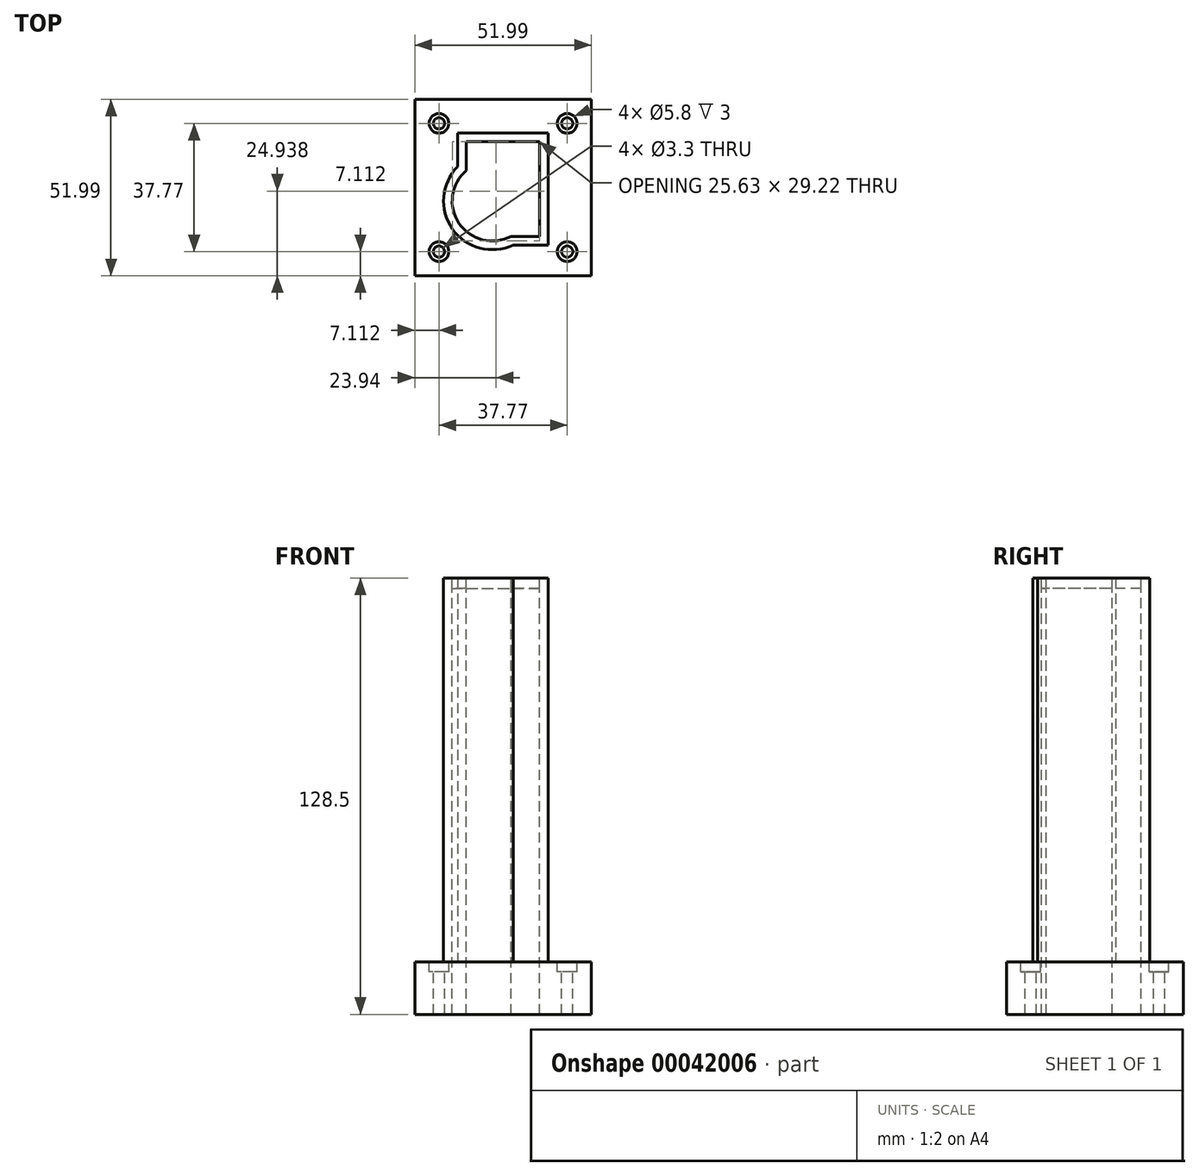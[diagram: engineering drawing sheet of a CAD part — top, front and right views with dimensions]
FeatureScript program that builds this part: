
annotation { "Feature Type Name" : "Feature", "Feature Type Description" : "" }
export const myFeature = defineFeature(function(context is Context, id is Id, definition is map)
    precondition{}
    {
        {
            var Q0;
            Q0=qCreatedBy(makeId("Top.planeOp"),FACE);
            var sketch = newSketch(context, id + "F0", { "sketchPlane" : qUnion([Q0])});
            skLineSegment(sketch, "E0.bottom", {"start": v(0, 0) * mm, "end": v(52, 0) * mm});
            skLineSegment(sketch, "E0.top", {"start": v(0, 52) * mm, "end": v(52, 52) * mm});
            skLineSegment(sketch, "E0.left", {"start": v(0, 0) * mm, "end": v(0, 52) * mm});
            skLineSegment(sketch, "E0.right", {"start": v(52, 0) * mm, "end": v(52, 52) * mm});
            skSolve(sketch);
        }
        {
            var Q0;
            Q0=qSketchRegion(id+"F0",true);
            extrude(context, id + "F1", {"entities" : qUnion([Q0]), "depth" : 15.5 * mm});
        }
        {
            var Q0;
            Q0=makeQuery(id+"F1.opExtrude","CAP_FACE",FACE,{"disambiguationData":[OSD([sQuery(id+"F0.wireOp",EDGE,"E0.bottom"),sQuery(id+"F0.wireOp",EDGE,"E0.top"),sQuery(id+"F0.wireOp",EDGE,"E0.left"),sQuery(id+"F0.wireOp",EDGE,"E0.right")])],"isStart":false});
            var sketch = newSketch(context, id + "F2", { "sketchPlane" : qUnion([Q0])});
            skCircle(sketch, "E1", {"center": v(7.11, 44.88) * mm, "radius": 2.9 * mm});
            skCircle(sketch, "E2", {"center": v(44.88, 44.88) * mm, "radius": 2.9 * mm});
            skCircle(sketch, "E3", {"center": v(7.11, 7.11) * mm, "radius": 2.9 * mm});
            skCircle(sketch, "E4", {"center": v(44.88, 7.11) * mm, "radius": 2.9 * mm});
            skSolve(sketch);
        }
        {
            var Q0;
            Q0=qSketchRegion(id+"F2",true);
            extrude(context, id + "F3", {"entities" : qUnion([Q0]), "operationType" : NewBodyOperationType.REMOVE, "oppositeDirection" : true, "depth" : 3 * mm});
        }
        {
            var Q0;
            Q0=makeQuery(id+"F3.boolean.opBoolean","COPY",FACE,{"derivedFrom":makeQuery(id+"F3.opExtrude","CAP_FACE",FACE,{"disambiguationData":[OSD([sQuery(id+"F2.wireOp",EDGE,"E1")])],"isStart":false})});
            var sketch = newSketch(context, id + "F4", { "sketchPlane" : qUnion([Q0])});
            skCircle(sketch, "E5", {"center": v(7.11, 44.88) * mm, "radius": 1.65 * mm});
            skSolve(sketch);
        }
        {
            var Q0;
            Q0=qSketchRegion(id+"F4",true);
            extrude(context, id + "F5", {"entities" : qUnion([Q0]), "operationType" : NewBodyOperationType.REMOVE, "endBound" : BoundingType.THROUGH_ALL, "oppositeDirection" : true, "depth" : 25.4 * mm});
        }
        {
            var Q0;
            Q0=makeQuery(id+"F3.boolean.opBoolean","COPY",FACE,{"derivedFrom":makeQuery(id+"F3.opExtrude","CAP_FACE",FACE,{"disambiguationData":[OSD([sQuery(id+"F2.wireOp",EDGE,"E2")])],"isStart":false})});
            var sketch = newSketch(context, id + "F6", { "sketchPlane" : qUnion([Q0])});
            skCircle(sketch, "E6", {"center": v(44.88, 44.88) * mm, "radius": 1.65 * mm});
            skSolve(sketch);
        }
        {
            var Q0;
            Q0=qSketchRegion(id+"F6",true);
            extrude(context, id + "F7", {"entities" : qUnion([Q0]), "operationType" : NewBodyOperationType.REMOVE, "endBound" : BoundingType.THROUGH_ALL, "oppositeDirection" : true, "depth" : 25.4 * mm});
        }
        {
            var Q0;
            Q0=makeQuery(id+"F3.boolean.opBoolean","COPY",FACE,{"derivedFrom":makeQuery(id+"F3.opExtrude","CAP_FACE",FACE,{"disambiguationData":[OSD([sQuery(id+"F2.wireOp",EDGE,"E3")])],"isStart":false})});
            var sketch = newSketch(context, id + "F8", { "sketchPlane" : qUnion([Q0])});
            skCircle(sketch, "E7", {"center": v(7.11, 7.11) * mm, "radius": 1.65 * mm});
            skSolve(sketch);
        }
        {
            var Q0;
            Q0=qSketchRegion(id+"F8",true);
            extrude(context, id + "F9", {"entities" : qUnion([Q0]), "operationType" : NewBodyOperationType.REMOVE, "endBound" : BoundingType.THROUGH_ALL, "oppositeDirection" : true, "depth" : 25.4 * mm});
        }
        {
            var Q0;
            Q0=makeQuery(id+"F3.boolean.opBoolean","COPY",FACE,{"derivedFrom":makeQuery(id+"F3.opExtrude","CAP_FACE",FACE,{"disambiguationData":[OSD([sQuery(id+"F2.wireOp",EDGE,"E4")])],"isStart":false})});
            var sketch = newSketch(context, id + "F10", { "sketchPlane" : qUnion([Q0])});
            skCircle(sketch, "E8", {"center": v(44.88, 7.11) * mm, "radius": 1.65 * mm});
            skSolve(sketch);
        }
        {
            var Q0;
            Q0=qSketchRegion(id+"F10",true);
            extrude(context, id + "F11", {"entities" : qUnion([Q0]), "operationType" : NewBodyOperationType.REMOVE, "endBound" : BoundingType.THROUGH_ALL, "oppositeDirection" : true, "depth" : 25.4 * mm});
        }
        {
            var Q0;
            Q0=makeQuery(id+"F1.opExtrude","CAP_FACE",FACE,{"disambiguationData":[OSD([sQuery(id+"F0.wireOp",EDGE,"E0.bottom"),sQuery(id+"F0.wireOp",EDGE,"E0.top"),sQuery(id+"F0.wireOp",EDGE,"E0.left"),sQuery(id+"F0.wireOp",EDGE,"E0.right")])],"isStart":false});
            var sketch = newSketch(context, id + "F12", { "sketchPlane" : qUnion([Q0])});
            skPoint(sketch, "E9.centerSnap0", {"position": v(18.87, 22.05) * mm});
            skPoint(sketch, "E10.orphan", {"position": v(18.87, 32.5) * mm});
            skPoint(sketch, "E11.orphan", {"position": v(18.87, 11.6) * mm});
            skPoint(sketch, "E12.end.orphan", {"position": v(15.39, 32.35) * mm});
            skLineSegment(sketch, "E13", {"start": v(15.16, 32.35) * mm, "end": v(15.39, 32.35) * mm});
            skLineSegment(sketch, "E14.0", {"start": v(39.3, 42.09) * mm, "end": v(39.3, 9.07) * mm});
            skLineSegment(sketch, "E14.1", {"start": v(12.62, 42.09) * mm, "end": v(39.3, 42.09) * mm});
            skLineSegment(sketch, "E14.2", {"start": v(39.3, 9.07) * mm, "end": v(28.94, 9.07) * mm});
            skArc(sketch, "E14.3", {"start": v(12.62, 32.14) * mm, "mid": v(11.11, 13.76) * mm, "end": v(28.94, 9.07) * mm});
            skLineSegment(sketch, "E14.4", {"start": v(12.62, 42.09) * mm, "end": v(12.62, 32.14) * mm});
            skSolve(sketch);
        }
        {
            var Q0;
            Q0=qSketchRegion(id+"F12",true);
            extrude(context, id + "F13", {"entities" : qUnion([Q0]), "operationType" : NewBodyOperationType.ADD, "depth" : 113 * mm});
        }
        {
            var Q0;
            Q0=makeQuery(id+"F13.opExtrude","CAP_FACE",FACE,{"disambiguationData":[OSD([sQuery(id+"F12.wireOp",EDGE,"E14.0"),sQuery(id+"F12.wireOp",EDGE,"E14.1"),sQuery(id+"F12.wireOp",EDGE,"E14.2"),sQuery(id+"F12.wireOp",EDGE,"E14.3"),sQuery(id+"F12.wireOp",EDGE,"E14.4")])],"isStart":false});
            var sketch = newSketch(context, id + "F14", { "sketchPlane" : qUnion([Q0])});
            skPoint(sketch, "E15.center.orphan", {"position": v(22.83, 22.05) * mm});
            skLineSegment(sketch, "E16.0", {"start": v(36.75, 39.55) * mm, "end": v(36.75, 11.6) * mm});
            skLineSegment(sketch, "E16.1", {"start": v(15.16, 39.55) * mm, "end": v(36.75, 39.55) * mm});
            skLineSegment(sketch, "E16.2", {"start": v(36.75, 11.6) * mm, "end": v(28.35, 11.6) * mm});
            skArc(sketch, "E16.3", {"start": v(15.16, 31.04) * mm, "mid": v(13.06, 15.42) * mm, "end": v(28.35, 11.6) * mm});
            skLineSegment(sketch, "E16.4", {"start": v(15.16, 39.55) * mm, "end": v(15.16, 31.04) * mm});
            skSolve(sketch);
        }
        {
            var Q0;
            Q0=qSketchRegion(id+"F14",true);
            extrude(context, id + "F15", {"entities" : qUnion([Q0]), "operationType" : NewBodyOperationType.REMOVE, "endBound" : BoundingType.THROUGH_ALL, "oppositeDirection" : true, "depth" : 25.4 * mm});
        }
        {
            var Q0;
            Q0=makeQuery(id+"F13.opExtrude","CAP_FACE",FACE,{"disambiguationData":[OSD([sQuery(id+"F12.wireOp",EDGE,"E14.0"),sQuery(id+"F12.wireOp",EDGE,"E14.1"),sQuery(id+"F12.wireOp",EDGE,"E14.2"),sQuery(id+"F12.wireOp",EDGE,"E14.3"),sQuery(id+"F12.wireOp",EDGE,"E14.4")])],"isStart":false});
            var sketch = newSketch(context, id + "F16", { "sketchPlane" : qUnion([Q0])});
            skLineSegment(sketch, "E17", {"start": v(15.16, 39.55) * mm, "end": v(36.75, 39.55) * mm});
            skLineSegment(sketch, "E18", {"start": v(36.75, 39.55) * mm, "end": v(36.75, 11.6) * mm});
            skLineSegment(sketch, "E19", {"start": v(36.75, 11.6) * mm, "end": v(28.35, 11.6) * mm});
            skLineSegment(sketch, "E20", {"start": v(15.16, 39.55) * mm, "end": v(15.16, 31.04) * mm});
            skArc(sketch, "E21", {"start": v(15.16, 31.04) * mm, "mid": v(13.06, 15.42) * mm, "end": v(28.35, 11.6) * mm});
            skSolve(sketch);
        }
        {
            var Q0;
            Q0=qSketchRegion(id+"F16",true);
            extrude(context, id + "F17", {"entities" : qUnion([Q0]), "oppositeDirection" : true, "depth" : 3.1 * mm});
        }
    });
